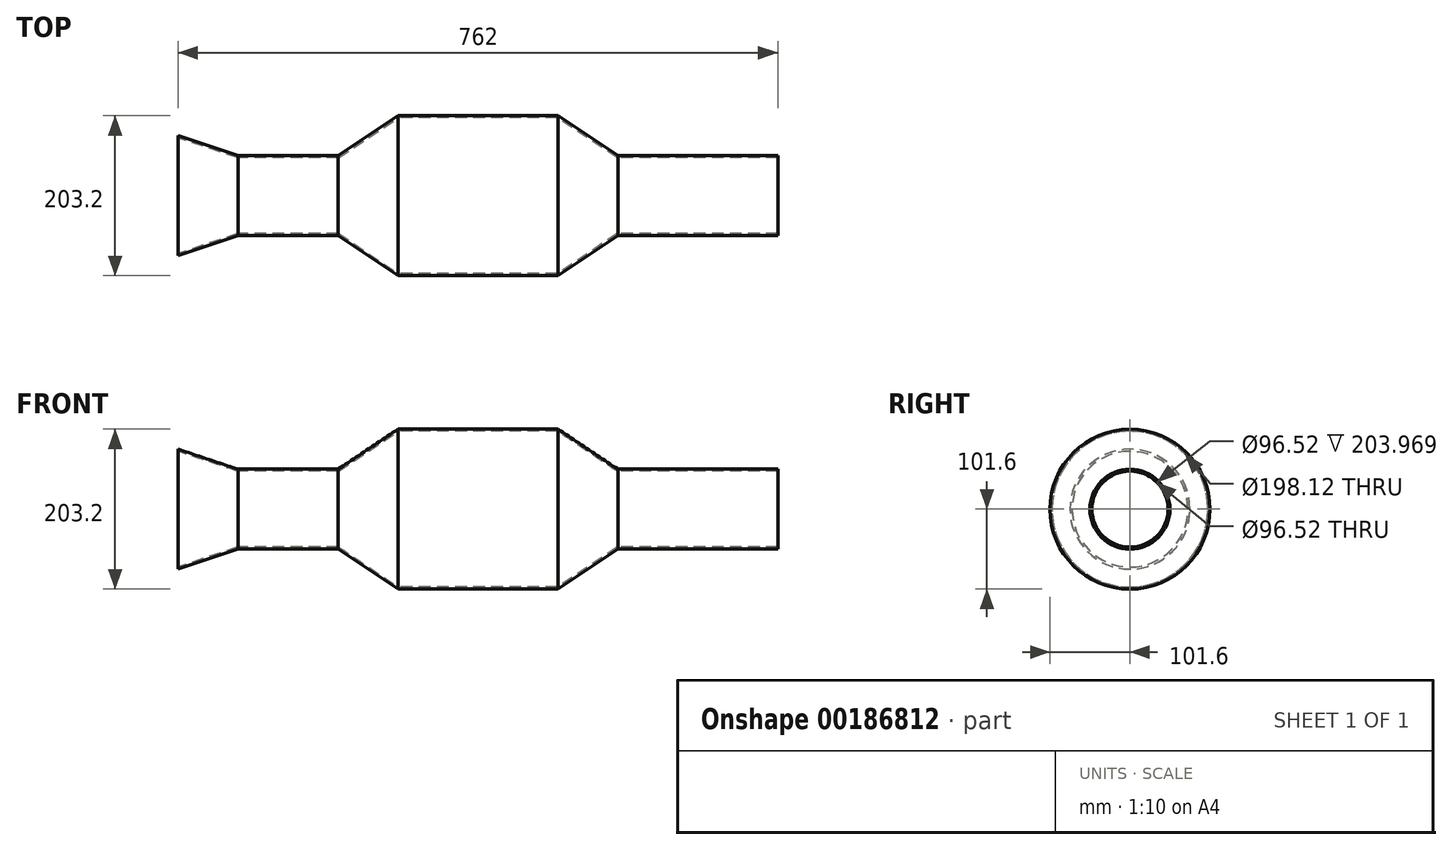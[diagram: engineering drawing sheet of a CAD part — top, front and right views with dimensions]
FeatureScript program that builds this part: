
annotation { "Feature Type Name" : "Feature", "Feature Type Description" : "" }
export const myFeature = defineFeature(function(context is Context, id is Id, definition is map)
    precondition{}
    {
        {
            var Q0;
            Q0=qCreatedBy(makeId("Front.planeOp"),FACE);
            var sketch = newSketch(context, id + "F0", { "sketchPlane" : qUnion([Q0])});
            skLineSegment(sketch, "E0", {"start": v(-381, 0) * mm, "end": v(381, 0) * mm, "construction": true});
            skLineSegment(sketch, "E1", {"start": v(381, 0) * mm, "end": v(381, 50.8) * mm});
            skLineSegment(sketch, "E2", {"start": v(381, 50.8) * mm, "end": v(177.8, 50.8) * mm});
            skLineSegment(sketch, "E3", {"start": v(177.8, 50.8) * mm, "end": v(101.6, 101.6) * mm});
            skLineSegment(sketch, "E4", {"start": v(101.6, 101.6) * mm, "end": v(-101.6, 101.6) * mm});
            skLineSegment(sketch, "E5", {"start": v(-101.6, 101.6) * mm, "end": v(-177.8, 50.8) * mm});
            skLineSegment(sketch, "E6", {"start": v(-177.8, 50.8) * mm, "end": v(-304.8, 50.8) * mm});
            skLineSegment(sketch, "E7", {"start": v(-304.8, 50.8) * mm, "end": v(-381, 76.2) * mm});
            skLineSegment(sketch, "E8", {"start": v(-381, 76.2) * mm, "end": v(-381, 0) * mm});
            skLineSegment(sketch, "E9", {"start": v(-381, 0) * mm, "end": v(381, 0) * mm});
            skSolve(sketch);
        }
        {
            var Q0;
            Q0 = qSketchRegion(id + "F0", true);
            var Q1;
            Q1=sQuery(id+"F0.wireOp",EDGE,"E0");
            revolve(context, id + "F1", {"entities" : qUnion([Q0]), "axis" : qUnion([Q1]), "revolveType" : RevolveType.FULL});
        }
        {
            var Q0;
            Q0=makeQuery(id+"F1.opRevolve","SWEPT_FACE",FACE,{"disambiguationData":[OSD([sQuery(id+"F0.wireOp",EDGE,"E8")])]});
            var Q1;
            Q1=makeQuery(id+"F1.opRevolve","SWEPT_FACE",FACE,{"disambiguationData":[OSD([sQuery(id+"F0.wireOp",EDGE,"E1")])]});
            shell(context, id + "F2", {"entities" : qUnion([Q0, Q1]), "thickness" : 2.54 * mm});
        }
    });
